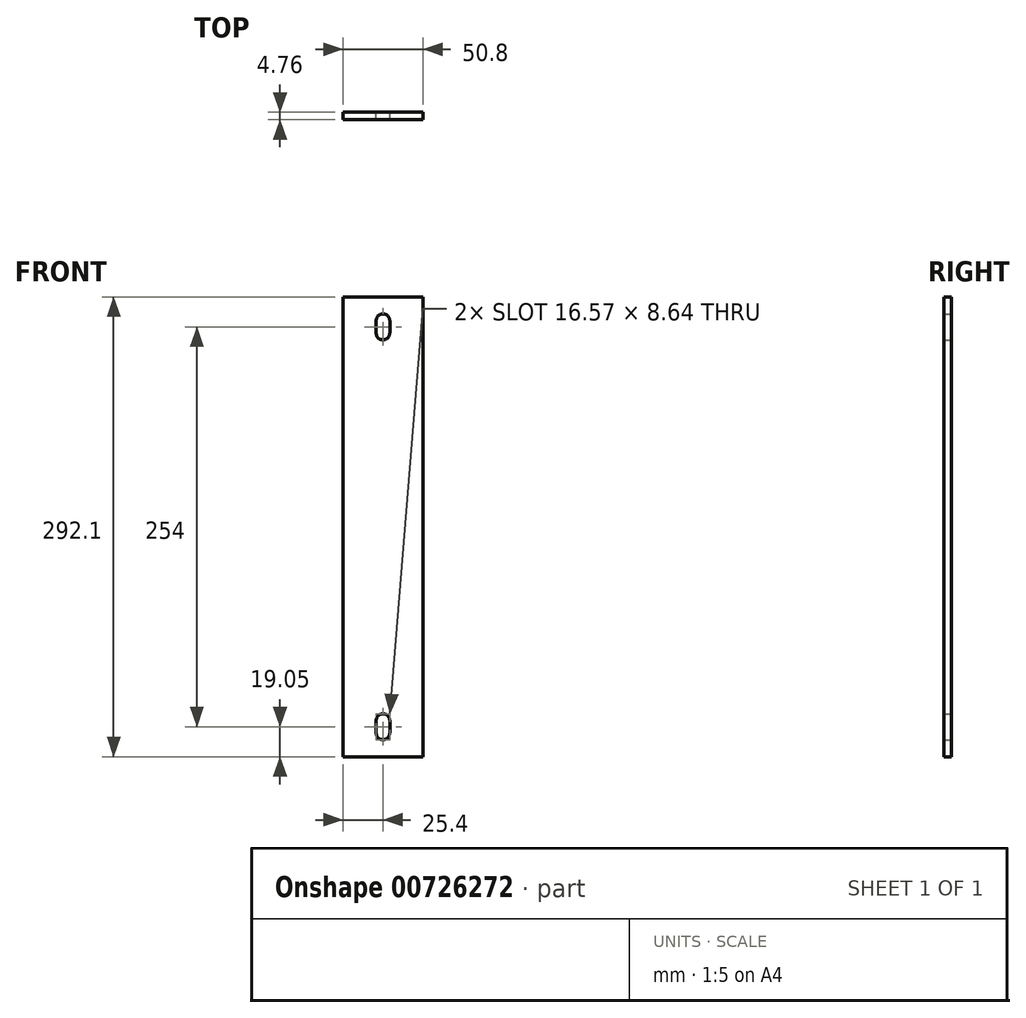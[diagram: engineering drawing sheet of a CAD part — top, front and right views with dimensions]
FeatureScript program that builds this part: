
annotation { "Feature Type Name" : "Feature", "Feature Type Description" : "" }
export const myFeature = defineFeature(function(context is Context, id is Id, definition is map)
    precondition{}
    {
        {
            var Q0;
            Q0=qCreatedBy(makeId("Front.planeOp"),FACE);
            var sketch = newSketch(context, id + "F0", { "sketchPlane" : qUnion([Q0])});
            skLineSegment(sketch, "E0.bottom", {"start": v(0, 0) * mm, "end": v(50.8, 0) * mm});
            skLineSegment(sketch, "E0.top", {"start": v(0, 292.1) * mm, "end": v(50.8, 292.1) * mm});
            skLineSegment(sketch, "E0.left", {"start": v(0, 0) * mm, "end": v(0, 292.1) * mm});
            skLineSegment(sketch, "E0.right", {"start": v(50.8, 0) * mm, "end": v(50.8, 292.1) * mm});
            skPoint(sketch, "E1.centerSnap0", {"position": v(25.4, 0) * mm});
            skPoint(sketch, "E2.centerSnap0", {"position": v(25.4, 292.1) * mm});
            skArc(sketch, "E3", {"start": v(21.08, 269.08) * mm, "mid": v(25.4, 264.76) * mm, "end": v(29.72, 269.08) * mm});
            skArc(sketch, "E4", {"start": v(21.08, 15.08) * mm, "mid": v(25.4, 10.76) * mm, "end": v(29.72, 15.08) * mm});
            skLineSegment(sketch, "E5", {"start": v(21.08, 277.02) * mm, "end": v(21.08, 269.08) * mm});
            skLineSegment(sketch, "E6", {"start": v(29.72, 277.02) * mm, "end": v(29.72, 269.08) * mm});
            skLineSegment(sketch, "E7", {"start": v(21.08, 23.02) * mm, "end": v(21.08, 15.08) * mm});
            skLineSegment(sketch, "E8", {"start": v(29.72, 23.02) * mm, "end": v(29.72, 15.08) * mm});
            skPoint(sketch, "E1.center.orphan", {"position": v(25.4, 19.05) * mm});
            skArc(sketch, "E9.trimOffspring", {"start": v(29.72, 23.02) * mm, "mid": v(25.4, 27.34) * mm, "end": v(21.08, 23.02) * mm});
            skArc(sketch, "E10.trimOffspring", {"start": v(29.72, 277.02) * mm, "mid": v(25.4, 281.34) * mm, "end": v(21.08, 277.02) * mm});
            skPoint(sketch, "E2.center.orphan", {"position": v(25.4, 273.05) * mm});
            skSolve(sketch);
        }
        {
            var Q0;
            Q0 = qSketchRegion(id + "F0", true);
            extrude(context, id + "F1", {"entities" : qUnion([Q0]), "depth" : 4.76 * mm, "offsetDistance" : 25.4 * mm});
        }
    });
